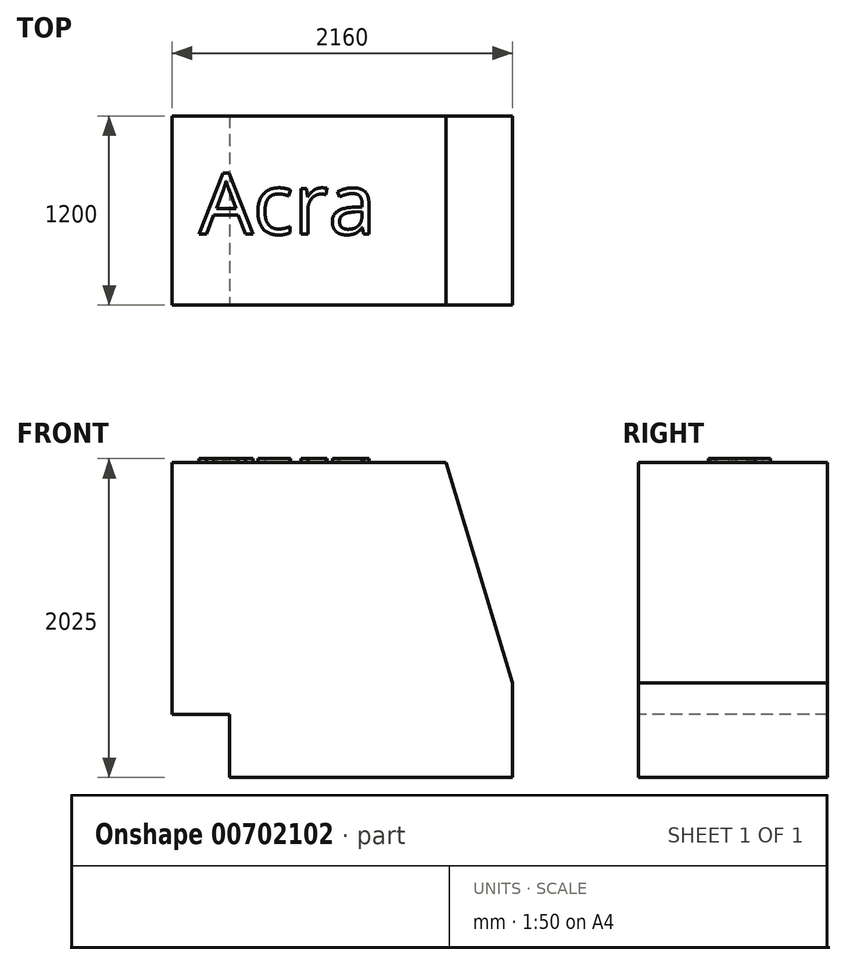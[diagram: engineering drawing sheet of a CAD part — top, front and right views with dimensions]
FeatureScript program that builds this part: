
annotation { "Feature Type Name" : "Feature", "Feature Type Description" : "" }
export const myFeature = defineFeature(function(context is Context, id is Id, definition is map)
    precondition{}
    {
        {
            var Q0;
            Q0=qCreatedBy(makeId("Top.planeOp"),FACE);
            var sketch = newSketch(context, id + "F0", { "sketchPlane" : qUnion([Q0])});
            skLineSegment(sketch, "E0.bottom", {"start": v(0, 0) * mm, "end": v(2160, 0) * mm});
            skLineSegment(sketch, "E0.top", {"start": v(0, -1200) * mm, "end": v(2160, -1200) * mm});
            skLineSegment(sketch, "E0.left", {"start": v(0, 0) * mm, "end": v(0, -1200) * mm});
            skLineSegment(sketch, "E0.right", {"start": v(2160, 0) * mm, "end": v(2160, -1200) * mm});
            skSolve(sketch);
        }
        {
            var Q0;
            Q0=makeQuery(id+"F0.imprint","IMPRINT",FACE,{"disambiguationData":[TD([[makeQuery(id+"F0.imprint","IMPRINT",EDGE,{"derivedFrom":sQuery(id+"F0.wireOp",EDGE,"E0.bottom")}),-1.0]])]});
            extrude(context, id + "F1", {"entities" : qUnion([Q0]), "depth" : 2000 * mm, "offsetDistance" : 25 * mm});
        }
        {
            var Q0;
            Q0=makeQuery(id+"F1.opExtrude","SWEPT_FACE",FACE,{"disambiguationData":[OSD([sQuery(id+"F0.wireOp",EDGE,"E0.top")])]});
            var sketch = newSketch(context, id + "F2", { "sketchPlane" : qUnion([Q0])});
            skLineSegment(sketch, "E1", {"start": v(2160, 600) * mm, "end": v(1738.05, 2000) * mm});
            skLineSegment(sketch, "E2", {"start": v(1738.05, 2000) * mm, "end": v(2160, 2000) * mm});
            skLineSegment(sketch, "E3", {"start": v(2160, 2000) * mm, "end": v(2160, 600) * mm});
            skSolve(sketch);
        }
        {
            var Q0;
            Q0=makeQuery(id+"F2.imprint","IMPRINT",FACE,{"disambiguationData":[TD([[makeQuery(id+"F2.imprint","IMPRINT",EDGE,{"derivedFrom":sQuery(id+"F2.wireOp",EDGE,"E1")}),-1.0]])]});
            extrude(context, id + "F3", {"entities" : qUnion([Q0]), "operationType" : NewBodyOperationType.REMOVE, "endBound" : BoundingType.THROUGH_ALL, "oppositeDirection" : true, "depth" : 25 * mm, "offsetDistance" : 25 * mm});
        }
        {
            var Q0;
            Q0=makeQuery(id+"F1.opExtrude","SWEPT_FACE",FACE,{"disambiguationData":[OSD([sQuery(id+"F0.wireOp",EDGE,"E0.top")])]});
            var sketch = newSketch(context, id + "F4", { "sketchPlane" : qUnion([Q0])});
            skLineSegment(sketch, "E4.bottom", {"start": v(0, 0) * mm, "end": v(365, 0) * mm});
            skLineSegment(sketch, "E4.top", {"start": v(0, 400) * mm, "end": v(365, 400) * mm});
            skLineSegment(sketch, "E4.left", {"start": v(0, 0) * mm, "end": v(0, 400) * mm});
            skLineSegment(sketch, "E4.right", {"start": v(365, 0) * mm, "end": v(365, 400) * mm});
            skSolve(sketch);
        }
        {
            var Q0;
            Q0=makeQuery(id+"F4.imprint","IMPRINT",FACE,{"disambiguationData":[TD([[makeQuery(id+"F4.imprint","IMPRINT",EDGE,{"derivedFrom":sQuery(id+"F4.wireOp",EDGE,"E4.bottom")}),1.0]])]});
            extrude(context, id + "F5", {"entities" : qUnion([Q0]), "operationType" : NewBodyOperationType.REMOVE, "endBound" : BoundingType.THROUGH_ALL, "oppositeDirection" : true, "depth" : 25 * mm, "offsetDistance" : 25 * mm});
        }
        {
            var Q0;
            Q0=makeQuery(id+"F1.opExtrude","CAP_FACE",FACE,{"disambiguationData":[OSD([sQuery(id+"F0.wireOp",EDGE,"E0.bottom"),sQuery(id+"F0.wireOp",EDGE,"E0.top"),sQuery(id+"F0.wireOp",EDGE,"E0.left"),sQuery(id+"F0.wireOp",EDGE,"E0.right")])],"isStart":false});
            var sketch = newSketch(context, id + "F6", { "sketchPlane" : qUnion([Q0])});
            skText(sketch, "E5", { "text": "Acra", "fontName": "OpenSans-Regular.ttf"});
            const initialGuessF6  = {"E5": [0.17053, -0.7498, 1, 0, 0.38947]};
            skSetInitialGuess(sketch, initialGuessF6);
            skSolve(sketch);
        }
        {
            var Q0;
            Q0 = qSketchRegion(id + "F6", true);
            extrude(context, id + "F7", {"entities" : qUnion([Q0]), "operationType" : NewBodyOperationType.ADD, "depth" : 25 * mm, "offsetDistance" : 25 * mm});
        }
    });
